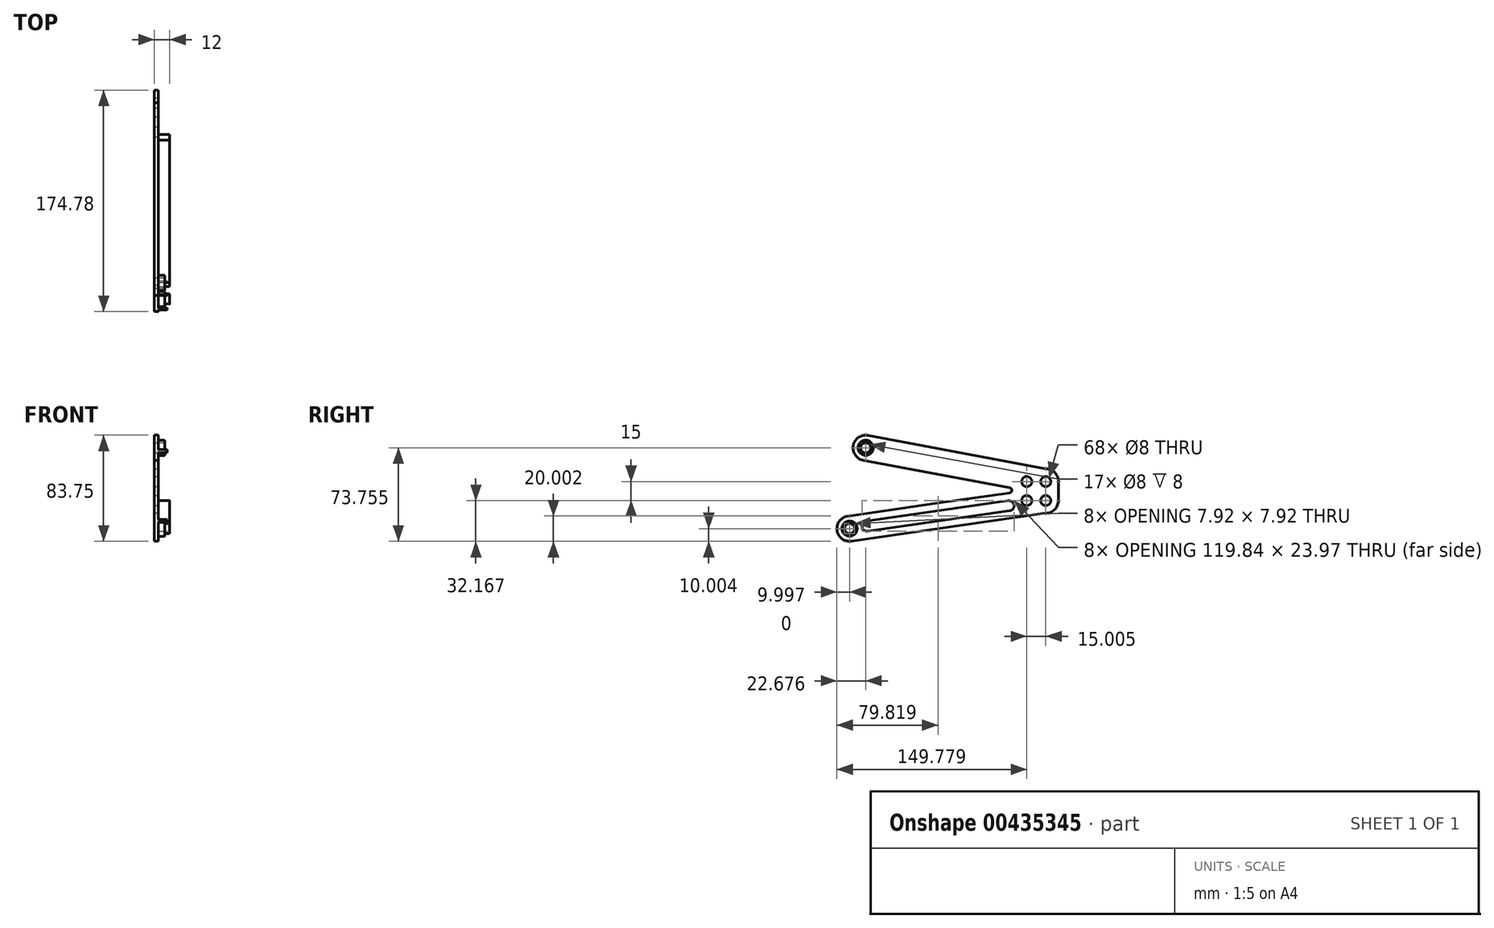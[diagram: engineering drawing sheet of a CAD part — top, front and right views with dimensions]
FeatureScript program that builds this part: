
annotation { "Feature Type Name" : "Feature", "Feature Type Description" : "" }
export const myFeature = defineFeature(function(context is Context, id is Id, definition is map)
    precondition{}
    {
        {
            var Q0;
            Q0=qCreatedBy(makeId("Right.planeOp"),FACE);
            var sketch = newSketch(context, id + "F0", { "sketchPlane" : qUnion([Q0])});
            skLineSegment(sketch, "E0", {"start": v(13, 42.77) * mm, "end": v(13, 42.8) * mm});
            skCircle(sketch, "E1", {"center": v(0.32, -20.98) * mm, "radius": 4 * mm});
            skCircle(sketch, "E2", {"center": v(13, 42.78) * mm, "radius": 4 * mm});
            skCircle(sketch, "E3", {"center": v(155.1, 16.19) * mm, "radius": 4 * mm});
            skCircle(sketch, "E4", {"center": v(140.1, 16.19) * mm, "radius": 4 * mm});
            skCircle(sketch, "E5", {"center": v(140.1, 1.19) * mm, "radius": 4 * mm});
            skCircle(sketch, "E6", {"center": v(155.1, 1.19) * mm, "radius": 4 * mm});
            skArc(sketch, "E7", {"start": v(14.85, 52.6) * mm, "mid": v(3.17, 44.57) * mm, "end": v(11.25, 32.93) * mm});
            skLineSegment(sketch, "E8", {"start": v(155.1, 26.23) * mm, "end": v(14.85, 52.6) * mm});
            skArc(sketch, "E9", {"start": v(-1.1, -11.08) * mm, "mid": v(-9.58, -22.4) * mm, "end": v(1.74, -30.87) * mm});
            skLineSegment(sketch, "E10", {"start": v(155.1, -8.81) * mm, "end": v(1.74, -30.87) * mm});
            skLineSegment(sketch, "E11", {"start": v(165.1, 16.19) * mm, "end": v(165.1, 1.19) * mm});
            skFitSpline(sketch, "E12", {"points": [v(-28.96, 68.23) * mm, v(-34.89, 65.58) * mm, v(-46.93, 48.54) * mm, v(-53.4, 30.04) * mm, v(-56.63, 9.77) * mm, v(-55.45, -6.98) * mm, v(-52.8, -22.84) * mm], "startDerivative": vector(-53.08, -12.9) * mm, "endDerivative": vector(16.86, -95.6) * mm});
            skLineSegment(sketch, "E13", {"start": v(-28.96, 55) * mm, "end": v(-43.33, 55) * mm});
            skLineSegment(sketch, "E14", {"start": v(-41.64, -8.74) * mm, "end": v(-55.19, -8.74) * mm});
            skFitSpline(sketch, "E15", {"points": [v(3.07, 41.61) * mm, v(6.66, 10.9) * mm, v(-8.41, -16.1) * mm], "startDerivative": vector(16.51, -63.29) * mm, "endDerivative": vector(-39.48, -52.14) * mm});
            skPoint(sketch, "E16.startSnap0", {"position": v(155.1, 6.69) * mm});
            skLineSegment(sketch, "E17", {"start": v(-1.1, -11.08) * mm, "end": v(108.52, 4.7) * mm});
            skLineSegment(sketch, "E18", {"start": v(69.77, -0.88) * mm, "end": v(126.65, 7.27) * mm});
            skLineSegment(sketch, "E19", {"start": v(13, 42.8) * mm, "end": v(13, 42.78) * mm});
            skLineSegment(sketch, "E20", {"start": v(11.25, 32.93) * mm, "end": v(126.74, 11.21) * mm});
            skArc(sketch, "E21.filletArc", {"start": v(126.65, 7.27) * mm, "mid": v(128.37, 9.2) * mm, "end": v(126.74, 11.21) * mm});
            skLineSegment(sketch, "E22", {"start": v(25.95, 36.27) * mm, "end": v(125.05, 17.23) * mm});
            skLineSegment(sketch, "E23", {"start": v(27.34, 43.6) * mm, "end": v(126.76, 24.94) * mm});
            skLineSegment(sketch, "E24", {"start": v(-0.25, -17.02) * mm, "end": v(-0.25, -17.02) * mm});
            skLineSegment(sketch, "E25", {"start": v(22.82, 40.89) * mm, "end": v(22.82, 40.89) * mm});
            skLineSegment(sketch, "E26", {"start": v(129.81, 20.07) * mm, "end": v(129.87, 20.36) * mm});
            skArc(sketch, "E27.filletArc", {"start": v(27.34, 43.6) * mm, "mid": v(24.49, 43.03) * mm, "end": v(22.79, 40.67) * mm});
            skArc(sketch, "E28.filletArc", {"start": v(22.79, 40.67) * mm, "mid": v(23.5, 37.84) * mm, "end": v(25.95, 36.27) * mm});
            skLineSegment(sketch, "E29", {"start": v(129.87, 20.36) * mm, "end": v(129.87, 20.34) * mm});
            skArc(sketch, "E30", {"start": v(126.76, 24.94) * mm, "mid": v(129.25, 23.29) * mm, "end": v(129.87, 20.36) * mm});
            skArc(sketch, "E31", {"start": v(125.05, 17.23) * mm, "mid": v(128.01, 17.68) * mm, "end": v(129.81, 20.07) * mm});
            skLineSegment(sketch, "E32", {"start": v(13.22, -15.09) * mm, "end": v(13.6, -15.03) * mm});
            skArc(sketch, "E33", {"start": v(14.64, -22.97) * mm, "mid": v(10.22, -19.7) * mm, "end": v(13.22, -15.09) * mm});
            skArc(sketch, "E34", {"start": v(126.66, -6.93) * mm, "mid": v(130.06, -2.43) * mm, "end": v(125.59, 1) * mm});
            skCircle(sketch, "E35", {"center": v(13, 42.77) * mm, "radius": 6 * mm});
            skCircle(sketch, "E36", {"center": v(0.32, -20.98) * mm, "radius": 6 * mm});
            skPoint(sketch, "E37.orphan", {"position": v(129.12, 16.47) * mm});
            skPoint(sketch, "E38.orphan", {"position": v(130.61, 24.22) * mm});
            skPoint(sketch, "E39.orphan", {"position": v(140.1, 8.69) * mm});
            skArc(sketch, "E40.trimOffspring", {"start": v(165.1, 16.19) * mm, "mid": v(162.18, 23.28) * mm, "end": v(155.1, 26.23) * mm});
            skPoint(sketch, "E41.trimOffspring.end.orphan", {"position": v(155.1, 12.19) * mm});
            skPoint(sketch, "E42.orphan", {"position": v(155.1, 20.19) * mm});
            skPoint(sketch, "E16.start.orphan", {"position": v(155.1, 6.19) * mm});
            skPoint(sketch, "E43.start.orphan", {"position": v(129.96, -2.45) * mm});
            skPoint(sketch, "E44.trimOffspring.start.orphan", {"position": v(129.4, 1.47) * mm});
            skPoint(sketch, "E45.trimOffspring.start.orphan", {"position": v(130.52, -6.37) * mm});
            skArc(sketch, "E46.trimOffspring", {"start": v(155.1, -8.81) * mm, "mid": v(162.17, -5.88) * mm, "end": v(165.1, 1.19) * mm});
            skPoint(sketch, "E47.trimOffspring.end.orphan", {"position": v(155.1, 5.14) * mm});
            skLineSegment(sketch, "E48.trimOffspring", {"start": v(155.1, 5.14) * mm, "end": v(155.1, 5.19) * mm});
            skPoint(sketch, "E49.start.orphan", {"position": v(155.1, -2.81) * mm});
            skLineSegment(sketch, "E50.trimOffspring", {"start": v(155.1, 1.19) * mm, "end": v(155.1, 1.19) * mm});
            skLineSegment(sketch, "E51.trimOffspring", {"start": v(13.22, -15.09) * mm, "end": v(125.59, 1) * mm});
            skLineSegment(sketch, "E52.trimOffspring", {"start": v(14.64, -22.97) * mm, "end": v(126.6, -6.94) * mm});
            skLineSegment(sketch, "E53", {"start": v(126.6, -6.94) * mm, "end": v(126.66, -6.93) * mm});
            skSolve(sketch);
        }
        {
            var Q0;
            {var subQ5=sQuery(id+"F0.wireOp",EDGE,"E8");Q0=makeQuery(id+"F0.imprint","IMPRINT",FACE,{"disambiguationData":[TD([[makeQuery(id+"F0.imprint","IMPRINT",EDGE,{"derivedFrom":subQ5}),1.0]])]});}
            var Q1;
            {var subQ3=sQuery(id+"F0.wireOp",EDGE,"E28.filletArc");Q1=makeQuery(id+"F0.imprint","IMPRINT",FACE,{"disambiguationData":[TD([[makeQuery(id+"F0.imprint","IMPRINT",EDGE,{"derivedFrom":subQ3}),-1.0]])]});}
            var Q2;
            {var subQ5=sQuery(id+"F0.wireOp",EDGE,"oFcgOY9X-3PXO-HXOB-FN7z-D7c9onW4hS7g");var subQ6=sQuery(id+"F0.wireOp",EDGE,"2sY4uV5q-Did9-YRWc-b1aj-hIykYh1mbjKz");var subQ7=makeQuery(id+"F0.imprint","INTERSECT",VERTEX,{"derivedFrom":[subQ6,subQ5]});Q2=makeQuery(id+"F0.imprint","IMPRINT",FACE,{"disambiguationData":[TD([[makeQuery(id+"F0.imprint","IMPRINT",EDGE,{"disambiguationData":[TD([[subQ7,-1.0]])],"derivedFrom":subQ6}),-1.0]])]});}
            var Q3;
            {var subQ0=sQuery(id+"F0.wireOp",EDGE,"VOfYyNmF-V63P-zWvf-osfN-JUbwS0qKl9GP");var subQ1=sQuery(id+"F0.wireOp",EDGE,"oFcgOY9X-3PXO-HXOB-FN7z-D7c9onW4hS7g");var subQ2=makeQuery(id+"F0.imprint","INTERSECT",VERTEX,{"disambiguationData":[OD(0.0)],"derivedFrom":[subQ1,subQ0]});Q3=makeQuery(id+"F0.imprint","IMPRINT",FACE,{"disambiguationData":[TD([[makeQuery(id+"F0.imprint","IMPRINT",EDGE,{"disambiguationData":[TD([[subQ2,-1.0]])],"derivedFrom":subQ1}),-1.0]])]});}
            var Q4;
            {var subQ0=sQuery(id+"F0.wireOp",EDGE,"oFcgOY9X-3PXO-HXOB-FN7z-D7c9onW4hS7g");var subQ1=makeQuery(id+"F0.imprint","INTERSECT",VERTEX,{"derivedFrom":[subQ0,sQuery(id+"F0.wireOp",EDGE,"E8")]});Q4=makeQuery(id+"F0.imprint","IMPRINT",FACE,{"disambiguationData":[TD([[makeQuery(id+"F0.imprint","IMPRINT",EDGE,{"disambiguationData":[TD([[subQ1,1.0]])],"derivedFrom":subQ0}),1.0]])]});}
            var Q5;
            {var subQ0=sQuery(id+"F0.wireOp",EDGE,"E3");var subQ1=sQuery(id+"F0.wireOp",EDGE,"2sY4uV5q-Did9-YRWc-b1aj-hIykYh1mbjKz");var subQ2=makeQuery(id+"F0.imprint","INTERSECT",VERTEX,{"derivedFrom":[subQ1,subQ0]});Q5=makeQuery(id+"F0.imprint","IMPRINT",FACE,{"disambiguationData":[TD([[makeQuery(id+"F0.imprint","IMPRINT",EDGE,{"disambiguationData":[TD([[subQ2,-1.0]])],"derivedFrom":subQ1}),-1.0]])]});}
            var Q6;
            {var subQ3=sQuery(id+"F0.wireOp",EDGE,"oFcgOY9X-3PXO-HXOB-FN7z-D7c9onW4hS7g");var subQ5=sQuery(id+"F0.wireOp",EDGE,"VOfYyNmF-V63P-zWvf-osfN-JUbwS0qKl9GP");var subQ6=makeQuery(id+"F0.imprint","INTERSECT",VERTEX,{"disambiguationData":[OD(1.0)],"derivedFrom":[subQ3,subQ5]});Q6=makeQuery(id+"F0.imprint","IMPRINT",FACE,{"disambiguationData":[TD([[makeQuery(id+"F0.imprint","IMPRINT",EDGE,{"disambiguationData":[TD([[subQ6,-1.0]])],"derivedFrom":subQ3}),1.0]])]});}
            var Q7;
            {var subQ0=sQuery(id+"F0.wireOp",EDGE,"E3");var subQ1=sQuery(id+"F0.wireOp",EDGE,"2sY4uV5q-Did9-YRWc-b1aj-hIykYh1mbjKz");var subQ2=makeQuery(id+"F0.imprint","INTERSECT",VERTEX,{"derivedFrom":[subQ1,subQ0]});Q7=makeQuery(id+"F0.imprint","IMPRINT",FACE,{"disambiguationData":[TD([[makeQuery(id+"F0.imprint","IMPRINT",EDGE,{"disambiguationData":[TD([[subQ2,-1.0]])],"derivedFrom":subQ1}),1.0]])]});}
            var Q8;
            {var subQ0=sQuery(id+"F0.wireOp",EDGE,"VOfYyNmF-V63P-zWvf-osfN-JUbwS0qKl9GP");var subQ1=sQuery(id+"F0.wireOp",EDGE,"oFcgOY9X-3PXO-HXOB-FN7z-D7c9onW4hS7g");var subQ2=makeQuery(id+"F0.imprint","INTERSECT",VERTEX,{"disambiguationData":[OD(0.0)],"derivedFrom":[subQ1,subQ0]});Q8=makeQuery(id+"F0.imprint","IMPRINT",FACE,{"disambiguationData":[TD([[makeQuery(id+"F0.imprint","IMPRINT",EDGE,{"disambiguationData":[TD([[subQ2,-1.0]])],"derivedFrom":subQ1}),1.0]])]});}
            var Q9;
            {var subQ0=sQuery(id+"F0.wireOp",EDGE,"VOfYyNmF-V63P-zWvf-osfN-JUbwS0qKl9GP");var subQ1=sQuery(id+"F0.wireOp",EDGE,"2sY4uV5q-Did9-YRWc-b1aj-hIykYh1mbjKz");var subQ2=makeQuery(id+"F0.imprint","INTERSECT",VERTEX,{"derivedFrom":[subQ1,subQ0]});Q9=makeQuery(id+"F0.imprint","IMPRINT",FACE,{"disambiguationData":[TD([[makeQuery(id+"F0.imprint","IMPRINT",EDGE,{"disambiguationData":[TD([[subQ2,-1.0]])],"derivedFrom":subQ1}),-1.0]])]});}
            var Q10;
            {var subQ3=sQuery(id+"F0.wireOp",EDGE,"E30");Q10=makeQuery(id+"F0.imprint","IMPRINT",FACE,{"disambiguationData":[TD([[makeQuery(id+"F0.imprint","IMPRINT",EDGE,{"derivedFrom":subQ3}),1.0]])]});}
            var Q11;
            {var subQ0=sQuery(id+"F0.wireOp",EDGE,"E26");var subQ1=sQuery(id+"F0.wireOp",EDGE,"E22");var subQ2=makeQuery(id+"F0.imprint","INTERSECT",VERTEX,{"derivedFrom":[subQ1,subQ0]});Q11=makeQuery(id+"F0.imprint","IMPRINT",FACE,{"disambiguationData":[TD([[makeQuery(id+"F0.imprint","IMPRINT",EDGE,{"disambiguationData":[TD([[subQ2,1.0]])],"derivedFrom":subQ1}),1.0]])]});}
            var Q12;
            {var subQ6=sQuery(id+"F0.wireOp",EDGE,"E23");var subQ8=sQuery(id+"F0.wireOp",EDGE,"VOfYyNmF-V63P-zWvf-osfN-JUbwS0qKl9GP");var subQ9=makeQuery(id+"F0.imprint","INTERSECT",VERTEX,{"disambiguationData":[OD(1.0)],"derivedFrom":[subQ8,subQ6]});Q12=makeQuery(id+"F0.imprint","IMPRINT",FACE,{"disambiguationData":[TD([[makeQuery(id+"F0.imprint","IMPRINT",EDGE,{"disambiguationData":[TD([[subQ9,-1.0]])],"derivedFrom":subQ8}),-1.0]])]});}
            var Q13;
            {var subQ7=sQuery(id+"F0.wireOp",EDGE,"E4");var subQ8=sQuery(id+"F0.wireOp",EDGE,"4AO0m6Q1-zq5p-SkaY-wgmb-Ein68IZjtmYg");var subQ9=makeQuery(id+"F0.imprint","INTERSECT",VERTEX,{"derivedFrom":[subQ8,subQ7]});Q13=makeQuery(id+"F0.imprint","IMPRINT",FACE,{"disambiguationData":[TD([[makeQuery(id+"F0.imprint","IMPRINT",EDGE,{"disambiguationData":[TD([[subQ9,-1.0]])],"derivedFrom":subQ8}),-1.0]])]});}
            var Q14;
            {var subQ0=sQuery(id+"F0.wireOp",EDGE,"E22");var subQ1=sQuery(id+"F0.wireOp",EDGE,"oFcgOY9X-3PXO-HXOB-FN7z-D7c9onW4hS7g");var subQ2=makeQuery(id+"F0.imprint","INTERSECT",VERTEX,{"derivedFrom":[subQ1,subQ0]});Q14=makeQuery(id+"F0.imprint","IMPRINT",FACE,{"disambiguationData":[TD([[makeQuery(id+"F0.imprint","IMPRINT",EDGE,{"disambiguationData":[TD([[subQ2,-1.0]])],"derivedFrom":subQ1}),1.0]])]});}
            var Q15;
            {var subQ0=sQuery(id+"F0.wireOp",EDGE,"VOfYyNmF-V63P-zWvf-osfN-JUbwS0qKl9GP");var subQ1=sQuery(id+"F0.wireOp",EDGE,"2sY4uV5q-Did9-YRWc-b1aj-hIykYh1mbjKz");var subQ2=makeQuery(id+"F0.imprint","INTERSECT",VERTEX,{"derivedFrom":[subQ1,subQ0]});Q15=makeQuery(id+"F0.imprint","IMPRINT",FACE,{"disambiguationData":[TD([[makeQuery(id+"F0.imprint","IMPRINT",EDGE,{"disambiguationData":[TD([[subQ2,-1.0]])],"derivedFrom":subQ1}),1.0]])]});}
            var Q16;
            {var subQ0=sQuery(id+"F0.wireOp",EDGE,"oFcgOY9X-3PXO-HXOB-FN7z-D7c9onW4hS7g");var subQ1=sQuery(id+"F0.wireOp",EDGE,"2sY4uV5q-Did9-YRWc-b1aj-hIykYh1mbjKz");var subQ2=makeQuery(id+"F0.imprint","INTERSECT",VERTEX,{"derivedFrom":[subQ1,subQ0]});Q16=makeQuery(id+"F0.imprint","IMPRINT",FACE,{"disambiguationData":[TD([[makeQuery(id+"F0.imprint","IMPRINT",EDGE,{"disambiguationData":[TD([[subQ2,-1.0]])],"derivedFrom":subQ1}),1.0]])]});}
            var Q17;
            {var subQ0=sQuery(id+"F0.wireOp",EDGE,"E11");Q17=makeQuery(id+"F0.imprint","IMPRINT",FACE,{"disambiguationData":[TD([[makeQuery(id+"F0.imprint","IMPRINT",EDGE,{"derivedFrom":subQ0}),-1.0]])]});}
            var Q18;
            {var subQ4=sQuery(id+"F0.wireOp",EDGE,"f9rGefkN-6VDd-lmMM-W2KQ-ElyYAtqZm0tD");var subQ5=sQuery(id+"F0.wireOp",EDGE,"E6");var subQ6=makeQuery(id+"F0.imprint","INTERSECT",VERTEX,{"derivedFrom":[subQ5,subQ4]});Q18=makeQuery(id+"F0.imprint","IMPRINT",FACE,{"disambiguationData":[TD([[makeQuery(id+"F0.imprint","IMPRINT",EDGE,{"disambiguationData":[TD([[subQ6,-1.0]])],"derivedFrom":subQ5}),-1.0]])]});}
            var Q19;
            {var subQ1=sQuery(id+"F0.wireOp",EDGE,"E49");var subQ3=sQuery(id+"F0.wireOp",EDGE,"ViXeE7RK-iWT2-vN9d-4oAN-SW0QdGtIy4yw");var subQ4=makeQuery(id+"F0.imprint","INTERSECT",VERTEX,{"derivedFrom":[subQ1,subQ3]});Q19=makeQuery(id+"F0.imprint","IMPRINT",FACE,{"disambiguationData":[TD([[makeQuery(id+"F0.imprint","IMPRINT",EDGE,{"disambiguationData":[TD([[subQ4,1.0]])],"derivedFrom":subQ3}),1.0]])]});}
            var Q20;
            {var subQ1=sQuery(id+"F0.wireOp",EDGE,"oFcgOY9X-3PXO-HXOB-FN7z-D7c9onW4hS7g");var subQ4=sQuery(id+"F0.wireOp",EDGE,"ViXeE7RK-iWT2-vN9d-4oAN-SW0QdGtIy4yw");var subQ7=makeQuery(id+"F0.imprint","INTERSECT",VERTEX,{"disambiguationData":[OD(0.0)],"derivedFrom":[subQ1,subQ4]});Q20=makeQuery(id+"F0.imprint","IMPRINT",FACE,{"disambiguationData":[TD([[makeQuery(id+"F0.imprint","IMPRINT",EDGE,{"disambiguationData":[TD([[subQ7,-1.0]])],"derivedFrom":subQ1}),1.0]])]});}
            var Q21;
            {var subQ0=sQuery(id+"F0.wireOp",EDGE,"xQ0mCiOl-8A36-HSTY-p9ta-LwGoWVGEagTe");var subQ1=sQuery(id+"F0.wireOp",EDGE,"uCMfiyUf-EAiu-ijRy-c0Gw-2XgW5qjE0rgX");var subQ2=makeQuery(id+"F0.imprint","INTERSECT",VERTEX,{"derivedFrom":[subQ1,subQ0]});Q21=makeQuery(id+"F0.imprint","IMPRINT",FACE,{"disambiguationData":[TD([[makeQuery(id+"F0.imprint","IMPRINT",EDGE,{"disambiguationData":[TD([[subQ2,-1.0]])],"derivedFrom":subQ1}),1.0]])]});}
            var Q22;
            {var subQ0=sQuery(id+"F0.wireOp",EDGE,"ViXeE7RK-iWT2-vN9d-4oAN-SW0QdGtIy4yw");var subQ1=sQuery(id+"F0.wireOp",EDGE,"uCMfiyUf-EAiu-ijRy-c0Gw-2XgW5qjE0rgX");var subQ2=makeQuery(id+"F0.imprint","INTERSECT",VERTEX,{"derivedFrom":[subQ1,subQ0]});Q22=makeQuery(id+"F0.imprint","IMPRINT",FACE,{"disambiguationData":[TD([[makeQuery(id+"F0.imprint","IMPRINT",EDGE,{"disambiguationData":[TD([[subQ2,-1.0]])],"derivedFrom":subQ1}),-1.0]])]});}
            var Q23;
            {var subQ0=sQuery(id+"F0.wireOp",EDGE,"ViXeE7RK-iWT2-vN9d-4oAN-SW0QdGtIy4yw");var subQ1=sQuery(id+"F0.wireOp",EDGE,"uCMfiyUf-EAiu-ijRy-c0Gw-2XgW5qjE0rgX");var subQ2=makeQuery(id+"F0.imprint","INTERSECT",VERTEX,{"derivedFrom":[subQ1,subQ0]});Q23=makeQuery(id+"F0.imprint","IMPRINT",FACE,{"disambiguationData":[TD([[makeQuery(id+"F0.imprint","IMPRINT",EDGE,{"disambiguationData":[TD([[subQ2,-1.0]])],"derivedFrom":subQ1}),1.0]])]});}
            var Q24;
            {var subQ1=sQuery(id+"F0.wireOp",EDGE,"4AO0m6Q1-zq5p-SkaY-wgmb-Ein68IZjtmYg");var subQ6=makeQuery(id+"F0.imprint","IMPRINT",VERTEX,{"derivedFrom":subQ1});Q24=makeQuery(id+"F0.imprint","IMPRINT",FACE,{"disambiguationData":[TD([[makeQuery(id+"F0.imprint","IMPRINT",EDGE,{"disambiguationData":[TD([[subQ6,1.0]])],"derivedFrom":subQ1}),1.0]])]});}
            var Q25;
            {var subQ0=sQuery(id+"F0.wireOp",EDGE,"VOfYyNmF-V63P-zWvf-osfN-JUbwS0qKl9GP");var subQ1=sQuery(id+"F0.wireOp",EDGE,"oFcgOY9X-3PXO-HXOB-FN7z-D7c9onW4hS7g");var subQ2=makeQuery(id+"F0.imprint","INTERSECT",VERTEX,{"disambiguationData":[OD(1.0)],"derivedFrom":[subQ1,subQ0]});Q25=makeQuery(id+"F0.imprint","IMPRINT",FACE,{"disambiguationData":[TD([[makeQuery(id+"F0.imprint","IMPRINT",EDGE,{"disambiguationData":[TD([[subQ2,-1.0]])],"derivedFrom":subQ1}),-1.0]])]});}
            var Q26;
            {var subQ0=sQuery(id+"F0.wireOp",EDGE,"ViXeE7RK-iWT2-vN9d-4oAN-SW0QdGtIy4yw");var subQ1=sQuery(id+"F0.wireOp",EDGE,"oFcgOY9X-3PXO-HXOB-FN7z-D7c9onW4hS7g");var subQ2=makeQuery(id+"F0.imprint","INTERSECT",VERTEX,{"disambiguationData":[OD(0.0)],"derivedFrom":[subQ1,subQ0]});Q26=makeQuery(id+"F0.imprint","IMPRINT",FACE,{"disambiguationData":[TD([[makeQuery(id+"F0.imprint","IMPRINT",EDGE,{"disambiguationData":[TD([[subQ2,-1.0]])],"derivedFrom":subQ1}),-1.0]])]});}
            var Q27;
            {var subQ6=sQuery(id+"F0.wireOp",EDGE,"VOfYyNmF-V63P-zWvf-osfN-JUbwS0qKl9GP");var subQ9=sQuery(id+"F0.wireOp",EDGE,"4AO0m6Q1-zq5p-SkaY-wgmb-Ein68IZjtmYg");var subQ12=makeQuery(id+"F0.imprint","INTERSECT",VERTEX,{"derivedFrom":[subQ9,subQ6]});Q27=makeQuery(id+"F0.imprint","IMPRINT",FACE,{"disambiguationData":[TD([[makeQuery(id+"F0.imprint","IMPRINT",EDGE,{"disambiguationData":[TD([[subQ12,-1.0]])],"derivedFrom":subQ9}),1.0]])]});}
            var Q28;
            {var subQ5=sQuery(id+"F0.wireOp",EDGE,"E4");var subQ6=sQuery(id+"F0.wireOp",EDGE,"4AO0m6Q1-zq5p-SkaY-wgmb-Ein68IZjtmYg");var subQ7=makeQuery(id+"F0.imprint","INTERSECT",VERTEX,{"derivedFrom":[subQ6,subQ5]});Q28=makeQuery(id+"F0.imprint","IMPRINT",FACE,{"disambiguationData":[TD([[makeQuery(id+"F0.imprint","IMPRINT",EDGE,{"disambiguationData":[TD([[subQ7,-1.0]])],"derivedFrom":subQ6}),1.0]])]});}
            var Q29;
            {var subQ5=sQuery(id+"F0.wireOp",EDGE,"E49");var subQ7=sQuery(id+"F0.wireOp",EDGE,"E6");var subQ8=makeQuery(id+"F0.imprint","INTERSECT",VERTEX,{"disambiguationData":[OD(1.0)],"derivedFrom":[subQ5,subQ7]});Q29=makeQuery(id+"F0.imprint","IMPRINT",FACE,{"disambiguationData":[TD([[makeQuery(id+"F0.imprint","IMPRINT",EDGE,{"disambiguationData":[TD([[subQ8,-1.0]])],"derivedFrom":subQ7}),-1.0]])]});}
            var Q30;
            {var subQ0=sQuery(id+"F0.wireOp",EDGE,"E16");var subQ1=sQuery(id+"F0.wireOp",EDGE,"ViXeE7RK-iWT2-vN9d-4oAN-SW0QdGtIy4yw");var subQ2=makeQuery(id+"F0.imprint","INTERSECT",VERTEX,{"derivedFrom":[subQ1,subQ0]});Q30=makeQuery(id+"F0.imprint","IMPRINT",FACE,{"disambiguationData":[TD([[makeQuery(id+"F0.imprint","IMPRINT",EDGE,{"disambiguationData":[TD([[subQ2,-1.0]])],"derivedFrom":subQ1}),1.0]])]});}
            var Q31;
            {var subQ0=sQuery(id+"F0.wireOp",EDGE,"xQ0mCiOl-8A36-HSTY-p9ta-LwGoWVGEagTe");var subQ1=sQuery(id+"F0.wireOp",EDGE,"uCMfiyUf-EAiu-ijRy-c0Gw-2XgW5qjE0rgX");var subQ2=makeQuery(id+"F0.imprint","INTERSECT",VERTEX,{"derivedFrom":[subQ1,subQ0]});Q31=makeQuery(id+"F0.imprint","IMPRINT",FACE,{"disambiguationData":[TD([[makeQuery(id+"F0.imprint","IMPRINT",EDGE,{"disambiguationData":[TD([[subQ2,-1.0]])],"derivedFrom":subQ1}),-1.0]])]});}
            var Q32;
            {var subQ0=sQuery(id+"F0.wireOp",EDGE,"f9rGefkN-6VDd-lmMM-W2KQ-ElyYAtqZm0tD");var subQ1=sQuery(id+"F0.wireOp",EDGE,"ViXeE7RK-iWT2-vN9d-4oAN-SW0QdGtIy4yw");var subQ2=makeQuery(id+"F0.imprint","INTERSECT",VERTEX,{"derivedFrom":[subQ1,subQ0]});Q32=makeQuery(id+"F0.imprint","IMPRINT",FACE,{"disambiguationData":[TD([[makeQuery(id+"F0.imprint","IMPRINT",EDGE,{"disambiguationData":[TD([[subQ2,-1.0]])],"derivedFrom":subQ1}),1.0]])]});}
            var Q33;
            {var subQ0=sQuery(id+"F0.wireOp",EDGE,"f9rGefkN-6VDd-lmMM-W2KQ-ElyYAtqZm0tD");var subQ1=sQuery(id+"F0.wireOp",EDGE,"ViXeE7RK-iWT2-vN9d-4oAN-SW0QdGtIy4yw");var subQ2=makeQuery(id+"F0.imprint","INTERSECT",VERTEX,{"derivedFrom":[subQ1,subQ0]});Q33=makeQuery(id+"F0.imprint","IMPRINT",FACE,{"disambiguationData":[TD([[makeQuery(id+"F0.imprint","IMPRINT",EDGE,{"disambiguationData":[TD([[subQ2,-1.0]])],"derivedFrom":subQ1}),-1.0]])]});}
            var Q34;
            {var subQ0=sQuery(id+"F0.wireOp",EDGE,"E5");var subQ1=sQuery(id+"F0.wireOp",EDGE,"uCMfiyUf-EAiu-ijRy-c0Gw-2XgW5qjE0rgX");var subQ2=makeQuery(id+"F0.imprint","INTERSECT",VERTEX,{"derivedFrom":[subQ1,subQ0]});Q34=makeQuery(id+"F0.imprint","IMPRINT",FACE,{"disambiguationData":[TD([[makeQuery(id+"F0.imprint","IMPRINT",EDGE,{"disambiguationData":[TD([[subQ2,-1.0]])],"derivedFrom":subQ1}),1.0]])]});}
            var Q35;
            {var subQ7=sQuery(id+"F0.wireOp",EDGE,"uCMfiyUf-EAiu-ijRy-c0Gw-2XgW5qjE0rgX");var subQ9=sQuery(id+"F0.wireOp",EDGE,"E5");var subQ11=makeQuery(id+"F0.imprint","INTERSECT",VERTEX,{"derivedFrom":[subQ7,subQ9]});Q35=makeQuery(id+"F0.imprint","IMPRINT",FACE,{"disambiguationData":[TD([[makeQuery(id+"F0.imprint","IMPRINT",EDGE,{"disambiguationData":[TD([[subQ11,-1.0]])],"derivedFrom":subQ7}),-1.0]])]});}
            var Q36;
            {var subQ0=sQuery(id+"F0.wireOp",EDGE,"PAjM3SSB-jkz3-Njnp-x1Lk-WQXFP04cyS6P");var subQ1=sQuery(id+"F0.wireOp",EDGE,"4AO0m6Q1-zq5p-SkaY-wgmb-Ein68IZjtmYg");var subQ2=makeQuery(id+"F0.imprint","INTERSECT",VERTEX,{"derivedFrom":[subQ1,subQ0]});Q36=makeQuery(id+"F0.imprint","IMPRINT",FACE,{"disambiguationData":[TD([[makeQuery(id+"F0.imprint","IMPRINT",EDGE,{"disambiguationData":[TD([[subQ2,-1.0]])],"derivedFrom":subQ1}),-1.0]])]});}
            var Q37;
            {var subQ0=sQuery(id+"F0.wireOp",EDGE,"4AO0m6Q1-zq5p-SkaY-wgmb-Ein68IZjtmYg");var subQ1=makeQuery(id+"F0.imprint","IMPRINT",VERTEX,{"derivedFrom":subQ0});Q37=makeQuery(id+"F0.imprint","IMPRINT",FACE,{"disambiguationData":[TD([[makeQuery(id+"F0.imprint","IMPRINT",EDGE,{"disambiguationData":[TD([[subQ1,1.0]])],"derivedFrom":subQ0}),-1.0]])]});}
            var Q38;
            {var subQ1=sQuery(id+"F0.wireOp",EDGE,"VOfYyNmF-V63P-zWvf-osfN-JUbwS0qKl9GP");var subQ5=sQuery(id+"F0.wireOp",EDGE,"4AO0m6Q1-zq5p-SkaY-wgmb-Ein68IZjtmYg");var subQ6=makeQuery(id+"F0.imprint","INTERSECT",VERTEX,{"derivedFrom":[subQ5,subQ1]});Q38=makeQuery(id+"F0.imprint","IMPRINT",FACE,{"disambiguationData":[TD([[makeQuery(id+"F0.imprint","IMPRINT",EDGE,{"disambiguationData":[TD([[subQ6,-1.0]])],"derivedFrom":subQ5}),-1.0]])]});}
            var Q39;
            {var subQ14=sQuery(id+"F0.wireOp",EDGE,"E18");Q39=makeQuery(id+"F0.imprint","IMPRINT",FACE,{"disambiguationData":[TD([[makeQuery(id+"F0.imprint","IMPRINT",EDGE,{"derivedFrom":subQ14}),-1.0]])]});}
            var Q40;
            {var subQ0=sQuery(id+"F0.wireOp",EDGE,"xYbgjqYA-apy8-lkM6-fzdP-q7lQpsCXUpBf");var subQ1=sQuery(id+"F0.wireOp",EDGE,"E24");var subQ2=makeQuery(id+"F0.imprint","INTERSECT",VERTEX,{"derivedFrom":[subQ1,subQ0]});Q40=makeQuery(id+"F0.imprint","IMPRINT",FACE,{"disambiguationData":[TD([[makeQuery(id+"F0.imprint","IMPRINT",EDGE,{"disambiguationData":[TD([[subQ2,1.0]])],"derivedFrom":subQ1}),-1.0]])]});}
            var Q41;
            {var subQ0=sQuery(id+"F0.wireOp",EDGE,"xYbgjqYA-apy8-lkM6-fzdP-q7lQpsCXUpBf");var subQ1=sQuery(id+"F0.wireOp",EDGE,"f9rGefkN-6VDd-lmMM-W2KQ-ElyYAtqZm0tD");var subQ2=makeQuery(id+"F0.imprint","INTERSECT",VERTEX,{"derivedFrom":[subQ1,subQ0]});Q41=makeQuery(id+"F0.imprint","IMPRINT",FACE,{"disambiguationData":[TD([[makeQuery(id+"F0.imprint","IMPRINT",EDGE,{"disambiguationData":[TD([[subQ2,1.0]])],"derivedFrom":subQ1}),1.0]])]});}
            var Q42;
            {var subQ3=sQuery(id+"F0.wireOp",EDGE,"xQ0mCiOl-8A36-HSTY-p9ta-LwGoWVGEagTe");var subQ5=sQuery(id+"F0.wireOp",EDGE,"E24");var subQ9=makeQuery(id+"F0.imprint","INTERSECT",VERTEX,{"disambiguationData":[OD(1.0)],"derivedFrom":[subQ3,subQ5]});Q42=makeQuery(id+"F0.imprint","IMPRINT",FACE,{"disambiguationData":[TD([[makeQuery(id+"F0.imprint","IMPRINT",EDGE,{"disambiguationData":[TD([[subQ9,-1.0]])],"derivedFrom":subQ3}),-1.0]])]});}
            var Q43;
            {var subQ5=sQuery(id+"F0.wireOp",EDGE,"E10");Q43=makeQuery(id+"F0.imprint","IMPRINT",FACE,{"disambiguationData":[TD([[makeQuery(id+"F0.imprint","IMPRINT",EDGE,{"derivedFrom":subQ5}),-1.0]])]});}
            var Q44;
            {var subQ0=sQuery(id+"F0.wireOp",EDGE,"E16");var subQ1=sQuery(id+"F0.wireOp",EDGE,"ViXeE7RK-iWT2-vN9d-4oAN-SW0QdGtIy4yw");var subQ2=makeQuery(id+"F0.imprint","INTERSECT",VERTEX,{"derivedFrom":[subQ1,subQ0]});Q44=makeQuery(id+"F0.imprint","IMPRINT",FACE,{"disambiguationData":[TD([[makeQuery(id+"F0.imprint","IMPRINT",EDGE,{"disambiguationData":[TD([[subQ2,1.0]])],"derivedFrom":subQ1}),1.0]])]});}
            var Q45;
            {var subQ0=sQuery(id+"F0.wireOp",EDGE,"E32");var subQ3=sQuery(id+"F0.wireOp",EDGE,"E33");var subQ5=makeQuery(id+"F0.imprint","INTERSECT",VERTEX,{"derivedFrom":[subQ0,subQ3]});Q45=makeQuery(id+"F0.imprint","IMPRINT",FACE,{"disambiguationData":[TD([[makeQuery(id+"F0.imprint","IMPRINT",EDGE,{"disambiguationData":[TD([[subQ5,1.0]])],"derivedFrom":subQ3}),1.0]])]});}
            var Q46;
            {var subQ0=sQuery(id+"F0.wireOp",EDGE,"FRKldS5F-ipiP-Z89M-aXC5-TEQAjwTjuqa6");var subQ1=sQuery(id+"F0.wireOp",EDGE,"f9rGefkN-6VDd-lmMM-W2KQ-ElyYAtqZm0tD");var subQ2=makeQuery(id+"F0.imprint","INTERSECT",VERTEX,{"derivedFrom":[subQ1,subQ0]});Q46=makeQuery(id+"F0.imprint","IMPRINT",FACE,{"disambiguationData":[TD([[makeQuery(id+"F0.imprint","IMPRINT",EDGE,{"disambiguationData":[TD([[subQ2,-1.0]])],"derivedFrom":subQ1}),1.0]])]});}
            var Q47;
            {var subQ0=sQuery(id+"F0.wireOp",EDGE,"E33");var subQ1=sQuery(id+"F0.wireOp",EDGE,"E9");var subQ2=makeQuery(id+"F0.imprint","INTERSECT",VERTEX,{"disambiguationData":[OD(1.0)],"derivedFrom":[subQ1,subQ0]});Q47=makeQuery(id+"F0.imprint","IMPRINT",FACE,{"disambiguationData":[TD([[makeQuery(id+"F0.imprint","IMPRINT",EDGE,{"disambiguationData":[TD([[subQ2,-1.0]])],"derivedFrom":subQ1}),1.0]])]});}
            var Q48;
            {var subQ0=sQuery(id+"F0.wireOp",EDGE,"E36");var subQ1=sQuery(id+"F0.wireOp",EDGE,"GlUIxNzo-LyGC-jXxr-hCHf-HWjp7udrCtmg");var subQ2=makeQuery(id+"F0.imprint","INTERSECT",VERTEX,{"derivedFrom":[subQ1,subQ0]});Q48=makeQuery(id+"F0.imprint","IMPRINT",FACE,{"disambiguationData":[TD([[makeQuery(id+"F0.imprint","IMPRINT",EDGE,{"disambiguationData":[TD([[subQ2,-1.0]])],"derivedFrom":subQ1}),-1.0]])]});}
            var Q49;
            {var subQ0=sQuery(id+"F0.wireOp",EDGE,"E36");var subQ1=sQuery(id+"F0.wireOp",EDGE,"GlUIxNzo-LyGC-jXxr-hCHf-HWjp7udrCtmg");var subQ2=makeQuery(id+"F0.imprint","INTERSECT",VERTEX,{"derivedFrom":[subQ1,subQ0]});Q49=makeQuery(id+"F0.imprint","IMPRINT",FACE,{"disambiguationData":[TD([[makeQuery(id+"F0.imprint","IMPRINT",EDGE,{"disambiguationData":[TD([[subQ2,-1.0]])],"derivedFrom":subQ1}),1.0]])]});}
            var Q50;
            {var subQ0=sQuery(id+"F0.wireOp",EDGE,"LZGu2tRq-eliU-WbUV-CiAU-Gii7tch6Fcpr");var subQ1=sQuery(id+"F0.wireOp",EDGE,"E9");var subQ2=makeQuery(id+"F0.imprint","INTERSECT",VERTEX,{"derivedFrom":[subQ1,subQ0]});Q50=makeQuery(id+"F0.imprint","IMPRINT",FACE,{"disambiguationData":[TD([[makeQuery(id+"F0.imprint","IMPRINT",EDGE,{"disambiguationData":[TD([[subQ2,1.0]])],"derivedFrom":subQ1}),1.0]])]});}
            var Q51;
            {var subQ0=sQuery(id+"F0.wireOp",EDGE,"E9");var subQ1=sQuery(id+"F0.wireOp",EDGE,"f39d60b4-8802-4296-94e9-3e73f228f90c");var subQ2=makeQuery(id+"F0.imprint","INTERSECT",VERTEX,{"derivedFrom":[subQ1,subQ0]});Q51=makeQuery(id+"F0.imprint","IMPRINT",FACE,{"disambiguationData":[TD([[makeQuery(id+"F0.imprint","IMPRINT",EDGE,{"disambiguationData":[TD([[subQ2,1.0]])],"derivedFrom":subQ1}),-1.0]])]});}
            var Q52;
            {var subQ0=sQuery(id+"F0.wireOp",EDGE,"E33");var subQ1=sQuery(id+"F0.wireOp",EDGE,"E9");var subQ2=makeQuery(id+"F0.imprint","INTERSECT",VERTEX,{"disambiguationData":[OD(1.0)],"derivedFrom":[subQ1,subQ0]});Q52=makeQuery(id+"F0.imprint","IMPRINT",FACE,{"disambiguationData":[TD([[makeQuery(id+"F0.imprint","IMPRINT",EDGE,{"disambiguationData":[TD([[subQ2,-1.0]])],"derivedFrom":subQ1}),-1.0]])]});}
            var Q53;
            {var subQ0=sQuery(id+"F0.wireOp",EDGE,"E33");var subQ1=sQuery(id+"F0.wireOp",EDGE,"E9");var subQ2=makeQuery(id+"F0.imprint","INTERSECT",VERTEX,{"disambiguationData":[OD(0.0)],"derivedFrom":[subQ1,subQ0]});Q53=makeQuery(id+"F0.imprint","IMPRINT",FACE,{"disambiguationData":[TD([[makeQuery(id+"F0.imprint","IMPRINT",EDGE,{"disambiguationData":[TD([[subQ2,1.0]])],"derivedFrom":subQ1}),-1.0]])]});}
            var Q54;
            {var subQ0=sQuery(id+"F0.wireOp",EDGE,"E9");var subQ1=sQuery(id+"F0.wireOp",EDGE,"GlUIxNzo-LyGC-jXxr-hCHf-HWjp7udrCtmg");var subQ2=makeQuery(id+"F0.imprint","INTERSECT",VERTEX,{"derivedFrom":[subQ1,subQ0]});Q54=makeQuery(id+"F0.imprint","IMPRINT",FACE,{"disambiguationData":[TD([[makeQuery(id+"F0.imprint","IMPRINT",EDGE,{"disambiguationData":[TD([[subQ2,-1.0]])],"derivedFrom":subQ1}),1.0]])]});}
            var Q55;
            {var subQ1=sQuery(id+"F0.wireOp",EDGE,"E9");var subQ3=sQuery(id+"F0.wireOp",EDGE,"f9rGefkN-6VDd-lmMM-W2KQ-ElyYAtqZm0tD");var subQ4=makeQuery(id+"F0.imprint","INTERSECT",VERTEX,{"derivedFrom":[subQ1,subQ3]});Q55=makeQuery(id+"F0.imprint","IMPRINT",FACE,{"disambiguationData":[TD([[makeQuery(id+"F0.imprint","IMPRINT",EDGE,{"disambiguationData":[TD([[subQ4,1.0]])],"derivedFrom":subQ3}),-1.0]])]});}
            var Q56;
            {var subQ0=sQuery(id+"F0.wireOp",EDGE,"E33");var subQ1=sQuery(id+"F0.wireOp",EDGE,"E9");var subQ2=makeQuery(id+"F0.imprint","INTERSECT",VERTEX,{"disambiguationData":[OD(0.0)],"derivedFrom":[subQ1,subQ0]});Q56=makeQuery(id+"F0.imprint","IMPRINT",FACE,{"disambiguationData":[TD([[makeQuery(id+"F0.imprint","IMPRINT",EDGE,{"disambiguationData":[TD([[subQ2,1.0]])],"derivedFrom":subQ1}),1.0]])]});}
            var Q57;
            {var subQ0=sQuery(id+"F0.wireOp",EDGE,"E9");var subQ1=sQuery(id+"F0.wireOp",EDGE,"f39d60b4-8802-4296-94e9-3e73f228f90c");var subQ2=makeQuery(id+"F0.imprint","INTERSECT",VERTEX,{"derivedFrom":[subQ1,subQ0]});Q57=makeQuery(id+"F0.imprint","IMPRINT",FACE,{"disambiguationData":[TD([[makeQuery(id+"F0.imprint","IMPRINT",EDGE,{"disambiguationData":[TD([[subQ2,1.0]])],"derivedFrom":subQ1}),1.0]])]});}
            var Q58;
            {var subQ3=sQuery(id+"F0.wireOp",EDGE,"E35");var subQ5=sQuery(id+"F0.wireOp",EDGE,"E19");var subQ8=makeQuery(id+"F0.imprint","INTERSECT",VERTEX,{"derivedFrom":[subQ5,subQ3]});Q58=makeQuery(id+"F0.imprint","IMPRINT",FACE,{"disambiguationData":[TD([[makeQuery(id+"F0.imprint","IMPRINT",EDGE,{"disambiguationData":[TD([[subQ8,1.0]])],"derivedFrom":subQ3}),-1.0]])]});}
            var Q59;
            {var subQ1=sQuery(id+"F0.wireOp",EDGE,"E7");var subQ5=makeQuery(id+"F0.imprint","IMPRINT",VERTEX,{"derivedFrom":subQ1});Q59=makeQuery(id+"F0.imprint","IMPRINT",FACE,{"disambiguationData":[TD([[makeQuery(id+"F0.imprint","IMPRINT",EDGE,{"disambiguationData":[TD([[subQ5,1.0]])],"derivedFrom":subQ1}),1.0]])]});}
            var Q60;
            {var subQ0=sQuery(id+"F0.wireOp",EDGE,"DL9onAKM-ir1j-rgHZ-QzGm-SpApc1QK6WWm");var subQ1=sQuery(id+"F0.wireOp",EDGE,"E7");var subQ2=makeQuery(id+"F0.imprint","INTERSECT",VERTEX,{"derivedFrom":[subQ1,subQ0]});Q60=makeQuery(id+"F0.imprint","IMPRINT",FACE,{"disambiguationData":[TD([[makeQuery(id+"F0.imprint","IMPRINT",EDGE,{"disambiguationData":[TD([[subQ2,-1.0]])],"derivedFrom":subQ1}),1.0]])]});}
            var Q61;
            {var subQ0=sQuery(id+"F0.wireOp",EDGE,"E7");var subQ1=sQuery(id+"F0.wireOp",EDGE,"E0");var subQ2=makeQuery(id+"F0.imprint","INTERSECT",VERTEX,{"derivedFrom":[subQ1,subQ0]});Q61=makeQuery(id+"F0.imprint","IMPRINT",FACE,{"disambiguationData":[TD([[makeQuery(id+"F0.imprint","IMPRINT",EDGE,{"disambiguationData":[TD([[subQ2,1.0]])],"derivedFrom":subQ1}),1.0]])]});}
            var Q62;
            {var subQ0=sQuery(id+"F0.wireOp",EDGE,"E7");var subQ1=sQuery(id+"F0.wireOp",EDGE,"E0");var subQ2=makeQuery(id+"F0.imprint","INTERSECT",VERTEX,{"derivedFrom":[subQ1,subQ0]});Q62=makeQuery(id+"F0.imprint","IMPRINT",FACE,{"disambiguationData":[TD([[makeQuery(id+"F0.imprint","IMPRINT",EDGE,{"disambiguationData":[TD([[subQ2,1.0]])],"derivedFrom":subQ1}),-1.0]])]});}
            var Q63;
            {var subQ1=sQuery(id+"F0.wireOp",EDGE,"E1");var subQ3=sQuery(id+"F0.wireOp",EDGE,"Nq1x8AvO-vsNP-dU8o-9KrR-YCJjJFsmixOr");var subQ4=makeQuery(id+"F0.imprint","INTERSECT",VERTEX,{"derivedFrom":[subQ1,subQ3]});Q63=makeQuery(id+"F0.imprint","IMPRINT",FACE,{"disambiguationData":[TD([[makeQuery(id+"F0.imprint","IMPRINT",EDGE,{"disambiguationData":[TD([[subQ4,-1.0]])],"derivedFrom":subQ3}),-1.0]])]});}
            var Q64;
            {var subQ0=sQuery(id+"F0.wireOp",EDGE,"E1");var subQ1=sQuery(id+"F0.wireOp",EDGE,"GlUIxNzo-LyGC-jXxr-hCHf-HWjp7udrCtmg");var subQ2=makeQuery(id+"F0.imprint","INTERSECT",VERTEX,{"derivedFrom":[subQ1,subQ0]});Q64=makeQuery(id+"F0.imprint","IMPRINT",FACE,{"disambiguationData":[TD([[makeQuery(id+"F0.imprint","IMPRINT",EDGE,{"disambiguationData":[TD([[subQ2,-1.0]])],"derivedFrom":subQ1}),-1.0]])]});}
            var Q65;
            {var subQ0=sQuery(id+"F0.wireOp",EDGE,"E24");var subQ1=sQuery(id+"F0.wireOp",EDGE,"GlUIxNzo-LyGC-jXxr-hCHf-HWjp7udrCtmg");var subQ2=makeQuery(id+"F0.imprint","INTERSECT",VERTEX,{"derivedFrom":[subQ1,subQ0]});Q65=makeQuery(id+"F0.imprint","IMPRINT",FACE,{"disambiguationData":[TD([[makeQuery(id+"F0.imprint","IMPRINT",EDGE,{"disambiguationData":[TD([[subQ2,-1.0]])],"derivedFrom":subQ1}),-1.0]])]});}
            var Q66;
            {var subQ0=sQuery(id+"F0.wireOp",EDGE,"E24");var subQ3=sQuery(id+"F0.wireOp",EDGE,"GlUIxNzo-LyGC-jXxr-hCHf-HWjp7udrCtmg");var subQ4=makeQuery(id+"F0.imprint","INTERSECT",VERTEX,{"derivedFrom":[subQ3,subQ0]});Q66=makeQuery(id+"F0.imprint","IMPRINT",FACE,{"disambiguationData":[TD([[makeQuery(id+"F0.imprint","IMPRINT",EDGE,{"disambiguationData":[TD([[subQ4,-1.0]])],"derivedFrom":subQ3}),1.0]])]});}
            var Q67;
            {var subQ0=sQuery(id+"F0.wireOp",EDGE,"NkdIEkJF-oaGE-cRA9-lhFt-wlPkOdRiEwhR");var subQ1=sQuery(id+"F0.wireOp",EDGE,"E1");var subQ2=makeQuery(id+"F0.imprint","INTERSECT",VERTEX,{"derivedFrom":[subQ1,subQ0]});Q67=makeQuery(id+"F0.imprint","IMPRINT",FACE,{"disambiguationData":[TD([[makeQuery(id+"F0.imprint","IMPRINT",EDGE,{"disambiguationData":[TD([[subQ2,-1.0]])],"derivedFrom":subQ1}),-1.0]])]});}
            var Q68;
            {var subQ0=sQuery(id+"F0.wireOp",EDGE,"E1");var subQ1=sQuery(id+"F0.wireOp",EDGE,"f39d60b4-8802-4296-94e9-3e73f228f90c");var subQ2=makeQuery(id+"F0.imprint","INTERSECT",VERTEX,{"derivedFrom":[subQ1,subQ0]});Q68=makeQuery(id+"F0.imprint","IMPRINT",FACE,{"disambiguationData":[TD([[makeQuery(id+"F0.imprint","IMPRINT",EDGE,{"disambiguationData":[TD([[subQ2,-1.0]])],"derivedFrom":subQ1}),-1.0]])]});}
            var Q69;
            {var subQ1=sQuery(id+"F0.wireOp",EDGE,"NkdIEkJF-oaGE-cRA9-lhFt-wlPkOdRiEwhR");var subQ3=sQuery(id+"F0.wireOp",EDGE,"E36");var subQ4=makeQuery(id+"F0.imprint","INTERSECT",VERTEX,{"disambiguationData":[OD(0.0)],"derivedFrom":[subQ1,subQ3]});Q69=makeQuery(id+"F0.imprint","IMPRINT",FACE,{"disambiguationData":[TD([[makeQuery(id+"F0.imprint","IMPRINT",EDGE,{"disambiguationData":[TD([[subQ4,-1.0]])],"derivedFrom":subQ3}),1.0]])]});}
            var Q70;
            {var subQ0=sQuery(id+"F0.wireOp",EDGE,"E1");var subQ1=sQuery(id+"F0.wireOp",EDGE,"f39d60b4-8802-4296-94e9-3e73f228f90c");var subQ2=makeQuery(id+"F0.imprint","INTERSECT",VERTEX,{"derivedFrom":[subQ1,subQ0]});Q70=makeQuery(id+"F0.imprint","IMPRINT",FACE,{"disambiguationData":[TD([[makeQuery(id+"F0.imprint","IMPRINT",EDGE,{"disambiguationData":[TD([[subQ2,-1.0]])],"derivedFrom":subQ1}),1.0]])]});}
            var Q71;
            {var subQ0=sQuery(id+"F0.wireOp",EDGE,"E1");var subQ1=sQuery(id+"F0.wireOp",EDGE,"GlUIxNzo-LyGC-jXxr-hCHf-HWjp7udrCtmg");var subQ2=makeQuery(id+"F0.imprint","INTERSECT",VERTEX,{"derivedFrom":[subQ1,subQ0]});Q71=makeQuery(id+"F0.imprint","IMPRINT",FACE,{"disambiguationData":[TD([[makeQuery(id+"F0.imprint","IMPRINT",EDGE,{"disambiguationData":[TD([[subQ2,-1.0]])],"derivedFrom":subQ1}),1.0]])]});}
            var Q72;
            {var subQ0=sQuery(id+"F0.wireOp",EDGE,"E35");var subQ1=sQuery(id+"F0.wireOp",EDGE,"GlUIxNzo-LyGC-jXxr-hCHf-HWjp7udrCtmg");var subQ2=makeQuery(id+"F0.imprint","INTERSECT",VERTEX,{"derivedFrom":[subQ1,subQ0]});Q72=makeQuery(id+"F0.imprint","IMPRINT",FACE,{"disambiguationData":[TD([[makeQuery(id+"F0.imprint","IMPRINT",EDGE,{"disambiguationData":[TD([[subQ2,-1.0]])],"derivedFrom":subQ1}),-1.0]])]});}
            var Q73;
            {var subQ0=sQuery(id+"F0.wireOp",EDGE,"E35");var subQ1=sQuery(id+"F0.wireOp",EDGE,"GlUIxNzo-LyGC-jXxr-hCHf-HWjp7udrCtmg");var subQ2=makeQuery(id+"F0.imprint","INTERSECT",VERTEX,{"derivedFrom":[subQ1,subQ0]});Q73=makeQuery(id+"F0.imprint","IMPRINT",FACE,{"disambiguationData":[TD([[makeQuery(id+"F0.imprint","IMPRINT",EDGE,{"disambiguationData":[TD([[subQ2,-1.0]])],"derivedFrom":subQ1}),1.0]])]});}
            var Q74;
            {var subQ0=sQuery(id+"F0.wireOp",EDGE,"E2");var subQ1=sQuery(id+"F0.wireOp",EDGE,"E0");var subQ2=makeQuery(id+"F0.imprint","INTERSECT",VERTEX,{"derivedFrom":[subQ1,subQ0]});Q74=makeQuery(id+"F0.imprint","IMPRINT",FACE,{"disambiguationData":[TD([[makeQuery(id+"F0.imprint","IMPRINT",EDGE,{"disambiguationData":[TD([[subQ2,-1.0]])],"derivedFrom":subQ1}),1.0]])]});}
            var Q75;
            {var subQ0=sQuery(id+"F0.wireOp",EDGE,"E2");var subQ1=sQuery(id+"F0.wireOp",EDGE,"E0");var subQ2=makeQuery(id+"F0.imprint","INTERSECT",VERTEX,{"derivedFrom":[subQ1,subQ0]});Q75=makeQuery(id+"F0.imprint","IMPRINT",FACE,{"disambiguationData":[TD([[makeQuery(id+"F0.imprint","IMPRINT",EDGE,{"disambiguationData":[TD([[subQ2,-1.0]])],"derivedFrom":subQ1}),-1.0]])]});}
            var Q76;
            {var subQ0=sQuery(id+"F0.wireOp",EDGE,"E19");var subQ1=sQuery(id+"F0.wireOp",EDGE,"E2");var subQ2=makeQuery(id+"F0.imprint","INTERSECT",VERTEX,{"derivedFrom":[subQ1,subQ0]});Q76=makeQuery(id+"F0.imprint","IMPRINT",FACE,{"disambiguationData":[TD([[makeQuery(id+"F0.imprint","IMPRINT",EDGE,{"disambiguationData":[TD([[subQ2,1.0]])],"derivedFrom":subQ1}),-1.0]])]});}
            var Q77;
            {var subQ5=sQuery(id+"F0.wireOp",EDGE,"E27.filletArc");Q77=makeQuery(id+"F0.imprint","IMPRINT",FACE,{"disambiguationData":[TD([[makeQuery(id+"F0.imprint","IMPRINT",EDGE,{"derivedFrom":subQ5}),1.0]])]});}
            var Q78;
            {var subQ11=sQuery(id+"F0.wireOp",EDGE,"TFe72Kd5-NPVX-2ggC-VSSe-iI2ohVqjuWcA");Q78=makeQuery(id+"F0.imprint","IMPRINT",FACE,{"disambiguationData":[TD([[makeQuery(id+"F0.imprint","IMPRINT",EDGE,{"derivedFrom":subQ11}),1.0]])]});}
            var Q79;
            {var subQ3=sQuery(id+"F0.wireOp",EDGE,"TFe72Kd5-NPVX-2ggC-VSSe-iI2ohVqjuWcA");Q79=makeQuery(id+"F0.imprint","IMPRINT",FACE,{"disambiguationData":[TD([[makeQuery(id+"F0.imprint","IMPRINT",EDGE,{"derivedFrom":subQ3}),-1.0]])]});}
            var Q80;
            {var subQ1=sQuery(id+"F0.wireOp",EDGE,"GlUIxNzo-LyGC-jXxr-hCHf-HWjp7udrCtmg");var subQ3=sQuery(id+"F0.wireOp",EDGE,"E17");var subQ4=makeQuery(id+"F0.imprint","INTERSECT",VERTEX,{"derivedFrom":[subQ1,subQ3]});Q80=makeQuery(id+"F0.imprint","IMPRINT",FACE,{"disambiguationData":[TD([[makeQuery(id+"F0.imprint","IMPRINT",EDGE,{"disambiguationData":[TD([[subQ4,-1.0]])],"derivedFrom":subQ1}),1.0]])]});}
            var Q81;
            {var subQ0=sQuery(id+"F0.wireOp",EDGE,"20426151-2042-401b-91cb-f49afc5df277.trimOffspring");var subQ1=sQuery(id+"F0.wireOp",EDGE,"E2");var subQ2=makeQuery(id+"F0.imprint","INTERSECT",VERTEX,{"derivedFrom":[subQ1,subQ0]});Q81=makeQuery(id+"F0.imprint","IMPRINT",FACE,{"disambiguationData":[TD([[makeQuery(id+"F0.imprint","IMPRINT",EDGE,{"disambiguationData":[TD([[subQ2,-1.0]])],"derivedFrom":subQ1}),-1.0]])]});}
            var Q82;
            {var subQ0=sQuery(id+"F0.wireOp",EDGE,"DL9onAKM-ir1j-rgHZ-QzGm-SpApc1QK6WWm");var subQ1=sQuery(id+"F0.wireOp",EDGE,"E2");var subQ2=makeQuery(id+"F0.imprint","INTERSECT",VERTEX,{"derivedFrom":[subQ1,subQ0]});Q82=makeQuery(id+"F0.imprint","IMPRINT",FACE,{"disambiguationData":[TD([[makeQuery(id+"F0.imprint","IMPRINT",EDGE,{"disambiguationData":[TD([[subQ2,-1.0]])],"derivedFrom":subQ1}),-1.0]])]});}
            var Q83;
            {var subQ0=sQuery(id+"F0.wireOp",EDGE,"E15");Q83=makeQuery(id+"F0.imprint","IMPRINT",FACE,{"disambiguationData":[TD([[makeQuery(id+"F0.imprint","IMPRINT",EDGE,{"derivedFrom":subQ0}),1.0]])]});}
            var Q84;
            Q84=makeQuery(id+"F0.imprint","IMPRINT",FACE,{"disambiguationData":[TD([[makeQuery(id+"F0.imprint","IMPRINT",EDGE,{"derivedFrom":sQuery(id+"F0.wireOp",EDGE,"E36")}),1.0]])]});
            var Q85;
            Q85=makeQuery(id+"F0.imprint","IMPRINT",FACE,{"disambiguationData":[TD([[makeQuery(id+"F0.imprint","IMPRINT",EDGE,{"derivedFrom":sQuery(id+"F0.wireOp",EDGE,"E2")}),-1.0]])]});
            var Q86;
            {var subQ3=sQuery(id+"F0.wireOp",EDGE,"E33");Q86=makeQuery(id+"F0.imprint","IMPRINT",FACE,{"disambiguationData":[TD([[makeQuery(id+"F0.imprint","IMPRINT",EDGE,{"derivedFrom":subQ3}),-1.0]])]});}
            extrude(context, id + "F1", {"entities" : qUnion([Q0, Q1, Q2, Q3, Q4, Q5, Q6, Q7, Q8, Q9, Q10, Q11, Q12, Q13, Q14, Q15, Q16, Q17, Q18, Q19, Q20, Q21, Q22, Q23, Q24, Q25, Q26, Q27, Q28, Q29, Q30, Q31, Q32, Q33, Q34, Q35, Q36, Q37, Q38, Q39, Q40, Q41, Q42, Q43, Q44, Q45, Q46, Q47, Q48, Q49, Q50, Q51, Q52, Q53, Q54, Q55, Q56, Q57, Q58, Q59, Q60, Q61, Q62, Q63, Q64, Q65, Q66, Q67, Q68, Q69, Q70, Q71, Q72, Q73, Q74, Q75, Q76, Q77, Q78, Q79, Q80, Q81, Q82, Q83, Q84, Q85, Q86]), "oppositeDirection" : true, "depth" : 12 * mm, "offsetDistance" : 25 * mm});
        }
        {
            var Q0;
            {var subQ0=sQuery(id+"F0.wireOp",EDGE,"E1");var subQ1=sQuery(id+"F0.wireOp",EDGE,"GlUIxNzo-LyGC-jXxr-hCHf-HWjp7udrCtmg");var subQ2=makeQuery(id+"F0.imprint","INTERSECT",VERTEX,{"derivedFrom":[subQ1,subQ0]});Q0=makeQuery(id+"F0.imprint","IMPRINT",FACE,{"disambiguationData":[TD([[makeQuery(id+"F0.imprint","IMPRINT",EDGE,{"disambiguationData":[TD([[subQ2,-1.0]])],"derivedFrom":subQ1}),1.0]])]});}
            var Q1;
            {var subQ0=sQuery(id+"F0.wireOp",EDGE,"E2");var subQ1=sQuery(id+"F0.wireOp",EDGE,"E0");var subQ2=makeQuery(id+"F0.imprint","INTERSECT",VERTEX,{"derivedFrom":[subQ1,subQ0]});Q1=makeQuery(id+"F0.imprint","IMPRINT",FACE,{"disambiguationData":[TD([[makeQuery(id+"F0.imprint","IMPRINT",EDGE,{"disambiguationData":[TD([[subQ2,-1.0]])],"derivedFrom":subQ1}),1.0]])]});}
            var Q2;
            {var subQ0=sQuery(id+"F0.wireOp",EDGE,"E24");var subQ1=sQuery(id+"F0.wireOp",EDGE,"GlUIxNzo-LyGC-jXxr-hCHf-HWjp7udrCtmg");var subQ2=makeQuery(id+"F0.imprint","INTERSECT",VERTEX,{"derivedFrom":[subQ1,subQ0]});Q2=makeQuery(id+"F0.imprint","IMPRINT",FACE,{"disambiguationData":[TD([[makeQuery(id+"F0.imprint","IMPRINT",EDGE,{"disambiguationData":[TD([[subQ2,-1.0]])],"derivedFrom":subQ1}),-1.0]])]});}
            var Q3;
            {var subQ0=sQuery(id+"F0.wireOp",EDGE,"E19");var subQ1=sQuery(id+"F0.wireOp",EDGE,"E2");var subQ2=makeQuery(id+"F0.imprint","INTERSECT",VERTEX,{"derivedFrom":[subQ1,subQ0]});Q3=makeQuery(id+"F0.imprint","IMPRINT",FACE,{"disambiguationData":[TD([[makeQuery(id+"F0.imprint","IMPRINT",EDGE,{"disambiguationData":[TD([[subQ2,1.0]])],"derivedFrom":subQ1}),-1.0]])]});}
            var Q4;
            {var subQ0=sQuery(id+"F0.wireOp",EDGE,"E2");var subQ1=sQuery(id+"F0.wireOp",EDGE,"E0");var subQ2=makeQuery(id+"F0.imprint","INTERSECT",VERTEX,{"derivedFrom":[subQ1,subQ0]});Q4=makeQuery(id+"F0.imprint","IMPRINT",FACE,{"disambiguationData":[TD([[makeQuery(id+"F0.imprint","IMPRINT",EDGE,{"disambiguationData":[TD([[subQ2,-1.0]])],"derivedFrom":subQ1}),-1.0]])]});}
            var Q5;
            {var subQ0=sQuery(id+"F0.wireOp",EDGE,"E24");var subQ3=sQuery(id+"F0.wireOp",EDGE,"GlUIxNzo-LyGC-jXxr-hCHf-HWjp7udrCtmg");var subQ4=makeQuery(id+"F0.imprint","INTERSECT",VERTEX,{"derivedFrom":[subQ3,subQ0]});Q5=makeQuery(id+"F0.imprint","IMPRINT",FACE,{"disambiguationData":[TD([[makeQuery(id+"F0.imprint","IMPRINT",EDGE,{"disambiguationData":[TD([[subQ4,-1.0]])],"derivedFrom":subQ3}),1.0]])]});}
            var Q6;
            {var subQ0=sQuery(id+"F0.wireOp",EDGE,"NkdIEkJF-oaGE-cRA9-lhFt-wlPkOdRiEwhR");var subQ1=sQuery(id+"F0.wireOp",EDGE,"E1");var subQ2=makeQuery(id+"F0.imprint","INTERSECT",VERTEX,{"derivedFrom":[subQ1,subQ0]});Q6=makeQuery(id+"F0.imprint","IMPRINT",FACE,{"disambiguationData":[TD([[makeQuery(id+"F0.imprint","IMPRINT",EDGE,{"disambiguationData":[TD([[subQ2,-1.0]])],"derivedFrom":subQ1}),-1.0]])]});}
            var Q7;
            {var subQ0=sQuery(id+"F0.wireOp",EDGE,"E1");var subQ1=sQuery(id+"F0.wireOp",EDGE,"f39d60b4-8802-4296-94e9-3e73f228f90c");var subQ2=makeQuery(id+"F0.imprint","INTERSECT",VERTEX,{"derivedFrom":[subQ1,subQ0]});Q7=makeQuery(id+"F0.imprint","IMPRINT",FACE,{"disambiguationData":[TD([[makeQuery(id+"F0.imprint","IMPRINT",EDGE,{"disambiguationData":[TD([[subQ2,-1.0]])],"derivedFrom":subQ1}),-1.0]])]});}
            var Q8;
            {var subQ0=sQuery(id+"F0.wireOp",EDGE,"E1");var subQ1=sQuery(id+"F0.wireOp",EDGE,"f39d60b4-8802-4296-94e9-3e73f228f90c");var subQ2=makeQuery(id+"F0.imprint","INTERSECT",VERTEX,{"derivedFrom":[subQ1,subQ0]});Q8=makeQuery(id+"F0.imprint","IMPRINT",FACE,{"disambiguationData":[TD([[makeQuery(id+"F0.imprint","IMPRINT",EDGE,{"disambiguationData":[TD([[subQ2,-1.0]])],"derivedFrom":subQ1}),1.0]])]});}
            var Q9;
            {var subQ1=sQuery(id+"F0.wireOp",EDGE,"NkdIEkJF-oaGE-cRA9-lhFt-wlPkOdRiEwhR");var subQ3=sQuery(id+"F0.wireOp",EDGE,"E36");var subQ4=makeQuery(id+"F0.imprint","INTERSECT",VERTEX,{"disambiguationData":[OD(0.0)],"derivedFrom":[subQ1,subQ3]});Q9=makeQuery(id+"F0.imprint","IMPRINT",FACE,{"disambiguationData":[TD([[makeQuery(id+"F0.imprint","IMPRINT",EDGE,{"disambiguationData":[TD([[subQ4,-1.0]])],"derivedFrom":subQ3}),1.0]])]});}
            var Q10;
            {var subQ1=sQuery(id+"F0.wireOp",EDGE,"E1");var subQ3=sQuery(id+"F0.wireOp",EDGE,"Nq1x8AvO-vsNP-dU8o-9KrR-YCJjJFsmixOr");var subQ4=makeQuery(id+"F0.imprint","INTERSECT",VERTEX,{"derivedFrom":[subQ1,subQ3]});Q10=makeQuery(id+"F0.imprint","IMPRINT",FACE,{"disambiguationData":[TD([[makeQuery(id+"F0.imprint","IMPRINT",EDGE,{"disambiguationData":[TD([[subQ4,-1.0]])],"derivedFrom":subQ3}),-1.0]])]});}
            var Q11;
            {var subQ1=sQuery(id+"F0.wireOp",EDGE,"E1");var subQ5=sQuery(id+"F0.wireOp",EDGE,"GlUIxNzo-LyGC-jXxr-hCHf-HWjp7udrCtmg");var subQ6=makeQuery(id+"F0.imprint","INTERSECT",VERTEX,{"derivedFrom":[subQ5,subQ1]});Q11=makeQuery(id+"F0.imprint","IMPRINT",FACE,{"disambiguationData":[TD([[makeQuery(id+"F0.imprint","IMPRINT",EDGE,{"disambiguationData":[TD([[subQ6,-1.0]])],"derivedFrom":subQ5}),-1.0]])]});}
            var Q12;
            {var subQ0=sQuery(id+"F0.wireOp",EDGE,"20426151-2042-401b-91cb-f49afc5df277.trimOffspring");var subQ1=sQuery(id+"F0.wireOp",EDGE,"E2");var subQ2=makeQuery(id+"F0.imprint","INTERSECT",VERTEX,{"derivedFrom":[subQ1,subQ0]});Q12=makeQuery(id+"F0.imprint","IMPRINT",FACE,{"disambiguationData":[TD([[makeQuery(id+"F0.imprint","IMPRINT",EDGE,{"disambiguationData":[TD([[subQ2,-1.0]])],"derivedFrom":subQ1}),-1.0]])]});}
            var Q13;
            {var subQ0=sQuery(id+"F0.wireOp",EDGE,"DL9onAKM-ir1j-rgHZ-QzGm-SpApc1QK6WWm");var subQ1=sQuery(id+"F0.wireOp",EDGE,"E2");var subQ2=makeQuery(id+"F0.imprint","INTERSECT",VERTEX,{"derivedFrom":[subQ1,subQ0]});Q13=makeQuery(id+"F0.imprint","IMPRINT",FACE,{"disambiguationData":[TD([[makeQuery(id+"F0.imprint","IMPRINT",EDGE,{"disambiguationData":[TD([[subQ2,-1.0]])],"derivedFrom":subQ1}),-1.0]])]});}
            var Q14;
            Q14=makeQuery(id+"F0.imprint","IMPRINT",FACE,{"disambiguationData":[TD([[makeQuery(id+"F0.imprint","IMPRINT",EDGE,{"derivedFrom":sQuery(id+"F0.wireOp",EDGE,"E2")}),-1.0]])]});
            var Q15;
            Q15=makeQuery(id+"F0.imprint","IMPRINT",FACE,{"disambiguationData":[TD([[makeQuery(id+"F0.imprint","IMPRINT",EDGE,{"derivedFrom":sQuery(id+"F0.wireOp",EDGE,"E36")}),1.0]])]});
            extrude(context, id + "F2", {"entities" : qUnion([Q0, Q1, Q2, Q3, Q4, Q5, Q6, Q7, Q8, Q9, Q10, Q11, Q12, Q13, Q14, Q15]), "operationType" : NewBodyOperationType.REMOVE, "oppositeDirection" : true, "depth" : 4 * mm, "offsetDistance" : 25 * mm});
        }
        {
            var Q0;
            {var subQ5=sQuery(id+"F0.wireOp",EDGE,"E27.filletArc");Q0=makeQuery(id+"F0.imprint","IMPRINT",FACE,{"disambiguationData":[TD([[makeQuery(id+"F0.imprint","IMPRINT",EDGE,{"derivedFrom":subQ5}),1.0]])]});}
            var Q1;
            {var subQ11=sQuery(id+"F0.wireOp",EDGE,"TFe72Kd5-NPVX-2ggC-VSSe-iI2ohVqjuWcA");Q1=makeQuery(id+"F0.imprint","IMPRINT",FACE,{"disambiguationData":[TD([[makeQuery(id+"F0.imprint","IMPRINT",EDGE,{"derivedFrom":subQ11}),1.0]])]});}
            var Q2;
            {var subQ3=sQuery(id+"F0.wireOp",EDGE,"TFe72Kd5-NPVX-2ggC-VSSe-iI2ohVqjuWcA");Q2=makeQuery(id+"F0.imprint","IMPRINT",FACE,{"disambiguationData":[TD([[makeQuery(id+"F0.imprint","IMPRINT",EDGE,{"derivedFrom":subQ3}),-1.0]])]});}
            var Q3;
            {var subQ1=sQuery(id+"F0.wireOp",EDGE,"GlUIxNzo-LyGC-jXxr-hCHf-HWjp7udrCtmg");var subQ3=sQuery(id+"F0.wireOp",EDGE,"E17");var subQ4=makeQuery(id+"F0.imprint","INTERSECT",VERTEX,{"derivedFrom":[subQ1,subQ3]});Q3=makeQuery(id+"F0.imprint","IMPRINT",FACE,{"disambiguationData":[TD([[makeQuery(id+"F0.imprint","IMPRINT",EDGE,{"disambiguationData":[TD([[subQ4,-1.0]])],"derivedFrom":subQ1}),1.0]])]});}
            var Q4;
            {var subQ3=sQuery(id+"F0.wireOp",EDGE,"E33");Q4=makeQuery(id+"F0.imprint","IMPRINT",FACE,{"disambiguationData":[TD([[makeQuery(id+"F0.imprint","IMPRINT",EDGE,{"derivedFrom":subQ3}),-1.0]])]});}
            extrude(context, id + "F3", {"entities" : qUnion([Q0, Q1, Q2, Q3, Q4]), "operationType" : NewBodyOperationType.REMOVE, "oppositeDirection" : true, "depth" : 9 * mm, "offsetDistance" : 25 * mm});
        }
        {
            var Q0;
            {var subQ0=sQuery(id+"F0.wireOp",EDGE,"E15");Q0=makeQuery(id+"F0.imprint","IMPRINT",FACE,{"disambiguationData":[TD([[makeQuery(id+"F0.imprint","IMPRINT",EDGE,{"derivedFrom":subQ0}),1.0]])]});}
            extrude(context, id + "F4", {"entities" : qUnion([Q0]), "operationType" : NewBodyOperationType.REMOVE, "oppositeDirection" : true, "depth" : 9 * mm, "offsetDistance" : 25 * mm});
        }
        {
            var Q0;
            Q0=makeQuery(id+"F1.opExtrude","CAP_EDGE",EDGE,{"disambiguationData":[OSD([sQuery(id+"F0.wireOp",EDGE,"E8")])],"isStart":true});
            var Q1;
            Q1=makeQuery(id+"F3.boolean.opBoolean","COPY",EDGE,{"derivedFrom":makeQuery(id+"F3.opExtrude","CAP_EDGE",EDGE,{"disambiguationData":[OSD([sQuery(id+"F0.wireOp",EDGE,"E23")])],"isStart":true})});
            var Q2;
            Q2=makeQuery(id+"F4.boolean.opBoolean","COPY",EDGE,{"derivedFrom":makeQuery(id+"F4.opExtrude","CAP_EDGE",EDGE,{"disambiguationData":[OSD([sQuery(id+"F0.wireOp",EDGE,"E20")])],"isStart":true})});
            var Q3;
            {var subQ0=sQuery(id+"F0.wireOp",EDGE,"E7");Q3=makeQuery(id+"F4.boolean.opBoolean","MERGE",EDGE,{"derivedFrom":[makeQuery(id+"F1.opExtrude","CAP_EDGE",EDGE,{"disambiguationData":[OSD([subQ0])],"isStart":true}),makeQuery(id+"F4.opExtrude","CAP_EDGE",EDGE,{"disambiguationData":[OSD([subQ0])],"isStart":true})]});}
            var Q4;
            {var subQ0=sQuery(id+"F0.wireOp",EDGE,"oFcgOY9X-3PXO-HXOB-FN7z-D7c9onW4hS7g");Q4=makeQuery(id+"F1.opExtrude","CAP_EDGE",EDGE,{"disambiguationData":[OSD([subQ0]),TDD([makeQuery(id+"F0.imprint","IMPRINT",EDGE,{"disambiguationData":[TD([[makeQuery(id+"F0.imprint","INTERSECT",VERTEX,{"derivedFrom":[subQ0,sQuery(id+"F0.wireOp",EDGE,"E8")]}),1.0]])],"derivedFrom":subQ0})])],"isStart":true});}
            var Q5;
            Q5=makeQuery(id+"F3.boolean.opBoolean","COPY",EDGE,{"derivedFrom":makeQuery(id+"F3.opExtrude","CAP_EDGE",EDGE,{"disambiguationData":[OSD([sQuery(id+"F0.wireOp",EDGE,"E31")])],"isStart":true})});
            var Q6;
            Q6=makeQuery(id+"F3.boolean.opBoolean","COPY",EDGE,{"derivedFrom":makeQuery(id+"F3.opExtrude","CAP_EDGE",EDGE,{"disambiguationData":[OSD([sQuery(id+"F0.wireOp",EDGE,"E30")])],"isStart":true})});
            var Q7;
            Q7=makeQuery(id+"F3.boolean.opBoolean","COPY",EDGE,{"derivedFrom":makeQuery(id+"F3.opExtrude","CAP_EDGE",EDGE,{"disambiguationData":[OSD([sQuery(id+"F0.wireOp",EDGE,"E27.filletArc")])],"isStart":true})});
            var Q8;
            Q8=makeQuery(id+"F3.boolean.opBoolean","COPY",EDGE,{"derivedFrom":makeQuery(id+"F3.opExtrude","CAP_EDGE",EDGE,{"disambiguationData":[OSD([sQuery(id+"F0.wireOp",EDGE,"E28.filletArc")])],"isStart":true})});
            var Q9;
            Q9=makeQuery(id+"F3.boolean.opBoolean","COPY",EDGE,{"derivedFrom":makeQuery(id+"F3.opExtrude","CAP_EDGE",EDGE,{"disambiguationData":[OSD([sQuery(id+"F0.wireOp",EDGE,"E22")])],"isStart":true})});
            var Q10;
            Q10=makeQuery(id+"F1.opExtrude","CAP_EDGE",EDGE,{"disambiguationData":[OSD([sQuery(id+"F0.wireOp",EDGE,"E11")])],"isStart":true});
            var Q11;
            Q11=makeQuery(id+"F1.opExtrude","CAP_EDGE",EDGE,{"disambiguationData":[OSD([sQuery(id+"F0.wireOp",EDGE,"E10")])],"isStart":true});
            var Q12;
            Q12=makeQuery(id+"F1.opExtrude","CAP_EDGE",EDGE,{"disambiguationData":[OSD([sQuery(id+"F0.wireOp",EDGE,"ViXeE7RK-iWT2-vN9d-4oAN-SW0QdGtIy4yw")])],"isStart":true});
            var Q13;
            Q13=makeQuery(id+"F4.boolean.opBoolean","COPY",EDGE,{"derivedFrom":makeQuery(id+"F4.opExtrude","CAP_EDGE",EDGE,{"disambiguationData":[OSD([sQuery(id+"F0.wireOp",EDGE,"E17")])],"isStart":true})});
            var Q14;
            Q14=makeQuery(id+"F4.boolean.opBoolean","COPY",EDGE,{"derivedFrom":makeQuery(id+"F4.opExtrude","CAP_EDGE",EDGE,{"disambiguationData":[OSD([sQuery(id+"F0.wireOp",EDGE,"E18")])],"isStart":true})});
            var Q15;
            Q15=makeQuery(id+"F4.boolean.opBoolean","COPY",EDGE,{"derivedFrom":makeQuery(id+"F4.opExtrude","CAP_EDGE",EDGE,{"disambiguationData":[OSD([sQuery(id+"F0.wireOp",EDGE,"E21.filletArc")])],"isStart":true})});
            var Q16;
            {var subQ0=sQuery(id+"F0.wireOp",EDGE,"E9");var subQ1=makeQuery(id+"F0.imprint","INTERSECT",VERTEX,{"derivedFrom":[sQuery(id+"F0.wireOp",EDGE,"f39d60b4-8802-4296-94e9-3e73f228f90c"),subQ0]});var subQ2=makeQuery(id+"F0.imprint","INTERSECT",VERTEX,{"derivedFrom":[subQ0,sQuery(id+"F0.wireOp",EDGE,"LZGu2tRq-eliU-WbUV-CiAU-Gii7tch6Fcpr")]});Q16=makeQuery(id+"F4.boolean.opBoolean","MERGE",EDGE,{"derivedFrom":[makeQuery(id+"F1.opExtrude","CAP_EDGE",EDGE,{"disambiguationData":[OSD([subQ0]),TDD([makeQuery(id+"F0.imprint","IMPRINT",EDGE,{"disambiguationData":[TD([[subQ2,1.0]])],"derivedFrom":subQ0}),makeQuery(id+"F0.imprint","IMPRINT",EDGE,{"disambiguationData":[TD([[subQ1,1.0]])],"derivedFrom":subQ0}),makeQuery(id+"F0.imprint","IMPRINT",EDGE,{"disambiguationData":[TD([[subQ1,-1.0]])],"derivedFrom":subQ0})])],"isStart":true}),makeQuery(id+"F4.opExtrude","CAP_EDGE",EDGE,{"disambiguationData":[OSD([subQ0])],"isStart":true})]});}
            var Q17;
            Q17=makeQuery(id+"F1.opExtrude","CAP_EDGE",EDGE,{"disambiguationData":[OSD([sQuery(id+"F0.wireOp",EDGE,"d876uiim-Pe67-rFSG-ZxDj-msHpbPFNuEjL")])],"isStart":true});
            var Q18;
            Q18=makeQuery(id+"F3.boolean.opBoolean","COPY",EDGE,{"derivedFrom":makeQuery(id+"F3.opExtrude","CAP_EDGE",EDGE,{"disambiguationData":[OSD([sQuery(id+"F0.wireOp",EDGE,"E24"),sQuery(id+"F0.wireOp",EDGE,"E32")])],"isStart":true})});
            var Q19;
            Q19=makeQuery(id+"F3.boolean.opBoolean","COPY",EDGE,{"derivedFrom":makeQuery(id+"F3.opExtrude","CAP_EDGE",EDGE,{"disambiguationData":[OSD([sQuery(id+"F0.wireOp",EDGE,"f9rGefkN-6VDd-lmMM-W2KQ-ElyYAtqZm0tD")])],"isStart":true})});
            var Q20;
            {var subQ0=sQuery(id+"F0.wireOp",EDGE,"E33");Q20=makeQuery(id+"F3.boolean.opBoolean","MERGE",EDGE,{"derivedFrom":[makeQuery(id+"F1.opExtrude","CAP_EDGE",EDGE,{"disambiguationData":[OSD([subQ0])],"isStart":true}),makeQuery(id+"F3.opExtrude","CAP_EDGE",EDGE,{"disambiguationData":[OSD([subQ0]),TDD([makeQuery(id+"F0.imprint","IMPRINT",EDGE,{"disambiguationData":[TD([[makeQuery(id+"F0.imprint","INTERSECT",VERTEX,{"derivedFrom":[sQuery(id+"F0.wireOp",EDGE,"f9rGefkN-6VDd-lmMM-W2KQ-ElyYAtqZm0tD"),subQ0]}),-1.0]])],"derivedFrom":subQ0})])],"isStart":true}),makeQuery(id+"F3.opExtrude","CAP_EDGE",EDGE,{"disambiguationData":[OSD([subQ0]),TDD([makeQuery(id+"F0.imprint","IMPRINT",EDGE,{"disambiguationData":[TD([[makeQuery(id+"F0.imprint","INTERSECT",VERTEX,{"derivedFrom":[sQuery(id+"F0.wireOp",EDGE,"E32"),subQ0]}),1.0]])],"derivedFrom":subQ0})])],"isStart":true})]});}
            var Q21;
            {var subQ0=sQuery(id+"F0.wireOp",EDGE,"E34");var subQ2=sQuery(id+"F0.wireOp",EDGE,"f9rGefkN-6VDd-lmMM-W2KQ-ElyYAtqZm0tD");var subQ3=makeQuery(id+"F0.imprint","INTERSECT",VERTEX,{"disambiguationData":[OD(1.0)],"derivedFrom":[subQ2,subQ0]});Q21=makeQuery(id+"F3.boolean.opBoolean","MERGE",EDGE,{"derivedFrom":[makeQuery(id+"F1.opExtrude","CAP_EDGE",EDGE,{"disambiguationData":[OSD([subQ0])],"isStart":true}),makeQuery(id+"F3.opExtrude","CAP_EDGE",EDGE,{"disambiguationData":[OSD([subQ0]),TDD([makeQuery(id+"F0.imprint","IMPRINT",EDGE,{"disambiguationData":[TD([[makeQuery(id+"F0.imprint","INTERSECT",VERTEX,{"disambiguationData":[OD(0.0)],"derivedFrom":[subQ2,subQ0]}),-1.0]])],"derivedFrom":subQ0}),makeQuery(id+"F0.imprint","IMPRINT",EDGE,{"disambiguationData":[TD([[subQ3,-1.0]])],"derivedFrom":subQ0})])],"isStart":true}),makeQuery(id+"F3.opExtrude","CAP_EDGE",EDGE,{"disambiguationData":[OSD([subQ0]),TDD([makeQuery(id+"F0.imprint","IMPRINT",EDGE,{"disambiguationData":[TD([[makeQuery(id+"F0.imprint","INTERSECT",VERTEX,{"derivedFrom":[sQuery(id+"F0.wireOp",EDGE,"E24"),subQ0]}),1.0]])],"derivedFrom":subQ0})])],"isStart":true})]});}
            var Q22;
            Q22=makeQuery(id+"F3.boolean.opBoolean","COPY",EDGE,{"derivedFrom":makeQuery(id+"F3.opExtrude","CAP_EDGE",EDGE,{"disambiguationData":[OSD([sQuery(id+"F0.wireOp",EDGE,"E51.trimOffspring")])],"isStart":true})});
            var Q23;
            Q23=makeQuery(id+"F3.boolean.opBoolean","COPY",EDGE,{"derivedFrom":makeQuery(id+"F3.opExtrude","CAP_EDGE",EDGE,{"disambiguationData":[OSD([sQuery(id+"F0.wireOp",EDGE,"E33")])],"isStart":true})});
            var Q24;
            Q24=makeQuery(id+"F3.boolean.opBoolean","COPY",EDGE,{"derivedFrom":makeQuery(id+"F3.opExtrude","CAP_EDGE",EDGE,{"disambiguationData":[OSD([sQuery(id+"F0.wireOp",EDGE,"E34")])],"isStart":true})});
            var Q25;
            Q25=makeQuery(id+"F3.boolean.opBoolean","COPY",EDGE,{"derivedFrom":makeQuery(id+"F3.opExtrude","CAP_EDGE",EDGE,{"disambiguationData":[OSD([sQuery(id+"F0.wireOp",EDGE,"E26"),sQuery(id+"F0.wireOp",EDGE,"E29")])],"isStart":true})});
            var Q26;
            Q26=makeQuery(id+"F3.boolean.opBoolean","COPY",EDGE,{"derivedFrom":makeQuery(id+"F3.opExtrude","CAP_EDGE",EDGE,{"disambiguationData":[OSD([sQuery(id+"F0.wireOp",EDGE,"E53")])],"isStart":true})});
            var Q27;
            Q27=makeQuery(id+"F3.boolean.opBoolean","COPY",EDGE,{"derivedFrom":makeQuery(id+"F3.opExtrude","CAP_EDGE",EDGE,{"disambiguationData":[OSD([sQuery(id+"F0.wireOp",EDGE,"E52.trimOffspring")])],"isStart":true})});
            var Q28;
            Q28=makeQuery(id+"F1.opExtrude","CAP_EDGE",EDGE,{"disambiguationData":[OSD([sQuery(id+"F0.wireOp",EDGE,"E40.trimOffspring")])],"isStart":true});
            chamfer(context, id + "F5", {"entities" : qUnion([Q0, Q1, Q2, Q3, Q4, Q5, Q6, Q7, Q8, Q9, Q10, Q11, Q12, Q13, Q14, Q15, Q16, Q17, Q18, Q19, Q20, Q21, Q22, Q23, Q24, Q25, Q26, Q27, Q28]), "width" : 2 * mm, "tangentPropagation" : true});
        }
    });
